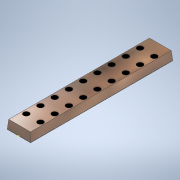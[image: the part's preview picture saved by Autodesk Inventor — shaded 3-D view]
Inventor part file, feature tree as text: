
AUTODESK INVENTOR PART (.ipt)
format: ipt  version: 2021 (Build 250183000, 183)  size: 168,960 bytes
history: native  units: in
note: dims shown in document units (in); Inventor stores cm internally (conversion verified against a paired STEP export)
features: sketch x4, extrude x3, mirror x1, pattern_linear x1, projected_geometry x1
ambient origin geometry x8: Origin, YZ Plane, XZ Plane, XY Plane, X Axis, Y Axis, Z Axis, Center Point
bodies: Solid1 (feature_tree)
feature tree (10):
  sketch  "Sketch1"  dims[d0=0.1614in d1=0.9843in]
  extrude  "Extrusion1"  Depth=0.9843in
  extrude  "Extrusion2"  Depth=0.0709in
  mirror  "Mirror1"
  extrude  "Extrusion3"  Depth=0.0014in
  pattern_linear  "Rectangular Pattern1"  Spacing1=0.0295in  [1 undecoded]
  sketch  "Sketch2"  dims[d2=0.0591in d3=-0.0344in d4=0.0709in]
  sketch  "Sketch3"  dims[d5=0.0014in d6=0.0in d7=0.0394in]
  projected_geometry  "Projected Loop1"
  sketch  "Sketch4"  dims[d8=0.0984in d9=0.0295in d10=0.0in d11=0.0in d12=3.5433in d14=0.0984in d15=0.7874in d17=0.0984in]
note: 1 required parameter value undecoded (feature->parameter linkage not recoverable at this tier; creation-order binding heuristic only, values carry confidence <= 0.55)
